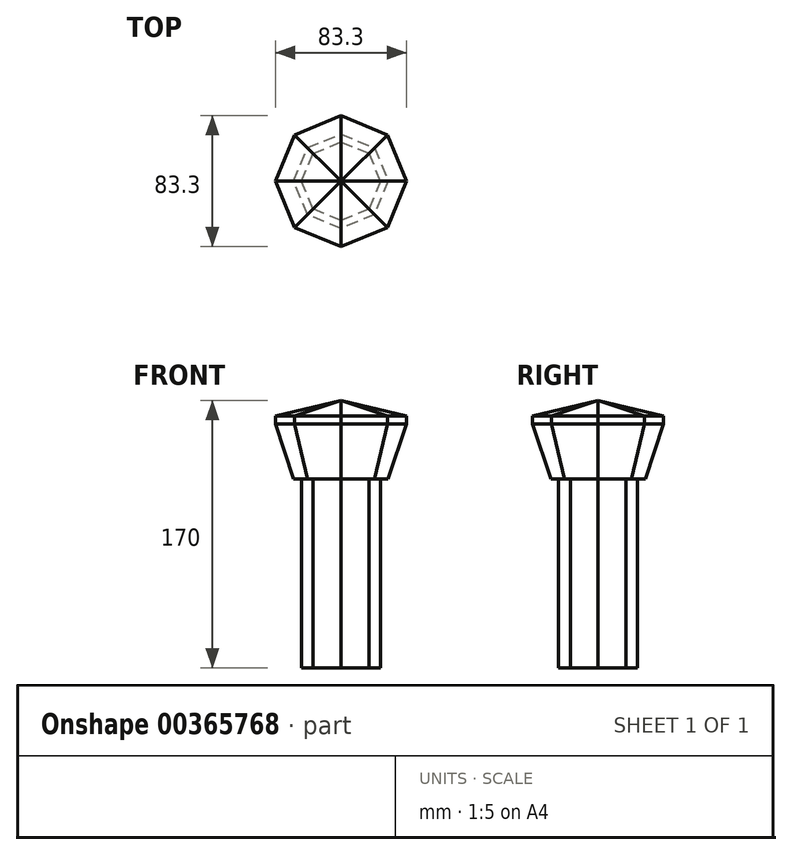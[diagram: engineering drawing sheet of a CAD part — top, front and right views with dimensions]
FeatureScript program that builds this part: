
annotation { "Feature Type Name" : "Feature", "Feature Type Description" : "" }
export const myFeature = defineFeature(function(context is Context, id is Id, definition is map)
    precondition{}
    {
        {
            var Q0;
            Q0=qCreatedBy(makeId("Top.planeOp"),FACE);
            cPlane(context, id + "F0", {"entities" : qUnion([Q0]), "cplaneType" : CPlaneType.OFFSET, "offset" : 120 * mm, "width" : 150 * mm, "height" : 150 * mm});
        }
        {
            var Q0;
            Q0=qCreatedBy(id+"F0.planeOp",FACE);
            cPlane(context, id + "F1", {"entities" : qUnion([Q0]), "cplaneType" : CPlaneType.OFFSET, "offset" : 35 * mm, "width" : 150 * mm, "height" : 150 * mm});
        }
        {
            var Q0;
            Q0=qCreatedBy(id+"F1.planeOp",FACE);
            cPlane(context, id + "F2", {"entities" : qUnion([Q0]), "cplaneType" : CPlaneType.OFFSET, "offset" : 5 * mm, "width" : 150 * mm, "height" : 150 * mm});
        }
        {
            var Q0;
            Q0=qCreatedBy(id+"F2.planeOp",FACE);
            cPlane(context, id + "F3", {"entities" : qUnion([Q0]), "cplaneType" : CPlaneType.OFFSET, "offset" : 10 * mm, "width" : 150 * mm, "height" : 150 * mm});
        }
        {
            var Q0;
            Q0=qCreatedBy(makeId("Top.planeOp"),FACE);
            var sketch = newSketch(context, id + "F4", { "sketchPlane" : qUnion([Q0])});
            skCircle(sketch, "E0.cCircle", {"center": v(0, 0) * mm, "radius": 25 * mm, "construction": true});
            skLineSegment(sketch, "E0.0", {"start": v(0, 25) * mm, "end": v(17.68, 17.68) * mm});
            skLineSegment(sketch, "E0.1", {"start": v(17.68, 17.68) * mm, "end": v(25, 0) * mm});
            skLineSegment(sketch, "E0.2", {"start": v(25, 0) * mm, "end": v(17.68, -17.68) * mm});
            skLineSegment(sketch, "E0.3", {"start": v(17.68, -17.68) * mm, "end": v(0, -25) * mm});
            skLineSegment(sketch, "E0.4", {"start": v(0, -25) * mm, "end": v(-17.68, -17.68) * mm});
            skLineSegment(sketch, "E0.5", {"start": v(-17.68, -17.68) * mm, "end": v(-25, 0) * mm});
            skLineSegment(sketch, "E0.6", {"start": v(-25, 0) * mm, "end": v(-17.68, 17.68) * mm});
            skLineSegment(sketch, "E0.7", {"start": v(-17.68, 17.68) * mm, "end": v(0, 25) * mm});
            skSolve(sketch);
        }
        {
            var Q0;
            Q0=makeQuery(id+"F4.imprint","IMPRINT",FACE,{"disambiguationData":[TD([[makeQuery(id+"F4.imprint","IMPRINT",EDGE,{"derivedFrom":sQuery(id+"F4.wireOp",EDGE,"E0.0")}),-1.0]])]});
            var Q1;
            Q1=qCreatedBy(id+"F0.planeOp",FACE);
            extrude(context, id + "F5", {"entities" : qUnion([Q0]), "endBound" : BoundingType.UP_TO_SURFACE, "endBoundEntityFace" : qUnion([Q1]), "depth" : 25 * mm});
        }
        {
            var Q0;
            Q0=qCreatedBy(id+"F0.planeOp",FACE);
            var sketch = newSketch(context, id + "F6", { "sketchPlane" : qUnion([Q0])});
            skCircle(sketch, "E1.cCircle", {"center": v(0, 0) * mm, "radius": 30 * mm, "construction": true});
            skLineSegment(sketch, "E1.0", {"start": v(0, 30) * mm, "end": v(21.21, 21.21) * mm});
            skLineSegment(sketch, "E1.1", {"start": v(21.21, 21.21) * mm, "end": v(30, 0) * mm});
            skLineSegment(sketch, "E1.2", {"start": v(30, 0) * mm, "end": v(21.21, -21.21) * mm});
            skLineSegment(sketch, "E1.3", {"start": v(21.21, -21.21) * mm, "end": v(0, -30) * mm});
            skLineSegment(sketch, "E1.4", {"start": v(0, -30) * mm, "end": v(-21.21, -21.21) * mm});
            skLineSegment(sketch, "E1.5", {"start": v(-21.21, -21.21) * mm, "end": v(-30, 0) * mm});
            skLineSegment(sketch, "E1.6", {"start": v(-30, 0) * mm, "end": v(-21.21, 21.21) * mm});
            skLineSegment(sketch, "E1.7", {"start": v(-21.21, 21.21) * mm, "end": v(0, 30) * mm});
            skSolve(sketch);
        }
        {
            var Q0;
            Q0=qCreatedBy(id+"F1.planeOp",FACE);
            var sketch = newSketch(context, id + "F7", { "sketchPlane" : qUnion([Q0])});
            skCircle(sketch, "E2.cCircle", {"center": v(0, 0) * mm, "radius": 41.65 * mm, "construction": true});
            skLineSegment(sketch, "E2.0", {"start": v(0, 41.65) * mm, "end": v(29.45, 29.45) * mm});
            skLineSegment(sketch, "E2.1", {"start": v(29.45, 29.45) * mm, "end": v(41.65, 0) * mm});
            skLineSegment(sketch, "E2.2", {"start": v(41.65, 0) * mm, "end": v(29.45, -29.45) * mm});
            skLineSegment(sketch, "E2.3", {"start": v(29.45, -29.45) * mm, "end": v(0, -41.65) * mm});
            skLineSegment(sketch, "E2.4", {"start": v(0, -41.65) * mm, "end": v(-29.45, -29.45) * mm});
            skLineSegment(sketch, "E2.5", {"start": v(-29.45, -29.45) * mm, "end": v(-41.65, 0) * mm});
            skLineSegment(sketch, "E2.6", {"start": v(-41.65, 0) * mm, "end": v(-29.45, 29.45) * mm});
            skLineSegment(sketch, "E2.7", {"start": v(-29.45, 29.45) * mm, "end": v(0, 41.65) * mm});
            skSolve(sketch);
        }
        {
            var Q1;
            Q1=makeQuery(id+"F6.imprint","IMPRINT",FACE,{"disambiguationData":[TD([[makeQuery(id+"F6.imprint","IMPRINT",EDGE,{"derivedFrom":sQuery(id+"F6.wireOp",EDGE,"E1.0")}),-1.0]])]});
            var Q2;
            Q2=makeQuery(id+"F7.imprint","IMPRINT",FACE,{"disambiguationData":[TD([[makeQuery(id+"F7.imprint","IMPRINT",EDGE,{"derivedFrom":sQuery(id+"F7.wireOp",EDGE,"E2.0")}),-1.0]])]});
            loft(context, id + "F8", {"operationType" : NewBodyOperationType.ADD, "sheetProfilesArray" : [{ "sheetProfileEntities" : qUnion([Q1]) }, { "sheetProfileEntities" : qUnion([Q2]) }]});
        }
        {
            var Q0;
            Q0=makeQuery(id+"F8.opLoft","CAP_FACE",FACE,{"disambiguationData":[OSD([makeQuery(id+"F7.imprint","IMPRINT",FACE,{"disambiguationData":[TD([[makeQuery(id+"F7.imprint","IMPRINT",EDGE,{"derivedFrom":sQuery(id+"F7.wireOp",EDGE,"E2.0")}),-1.0]])]})])],"isStart":true});
            var Q1;
            Q1=qCreatedBy(id+"F2.planeOp",FACE);
            extrude(context, id + "F9", {"entities" : qUnion([Q0]), "operationType" : NewBodyOperationType.ADD, "endBound" : BoundingType.UP_TO_SURFACE, "endBoundEntityFace" : qUnion([Q1]), "depth" : 25 * mm});
        }
        {
            var Q0;
            Q0=qCreatedBy(id+"F3.planeOp",FACE);
            var sketch = newSketch(context, id + "F10", { "sketchPlane" : qUnion([Q0])});
            skPoint(sketch, "E3", {"position": v(0, 0) * mm});
            skSolve(sketch);
        }
        {
            var Q1;
            Q1=makeQuery(id+"F9.opExtrude","CAP_FACE",FACE,{"disambiguationData":[OSD([makeQuery(id+"F7.imprint","IMPRINT",FACE,{"disambiguationData":[TD([[makeQuery(id+"F7.imprint","IMPRINT",EDGE,{"derivedFrom":sQuery(id+"F7.wireOp",EDGE,"E2.0")}),-1.0]])]})])],"isStart":false});
            var Q2;
            Q2=sQuery(id+"F10.wireOp",VERTEX,"E3");
            loft(context, id + "F11", {"operationType" : NewBodyOperationType.ADD, "sheetProfilesArray" : [{ "sheetProfileEntities" : qUnion([Q1]) }, { "sheetProfileEntities" : qUnion([Q2]) }]});
        }
    });
